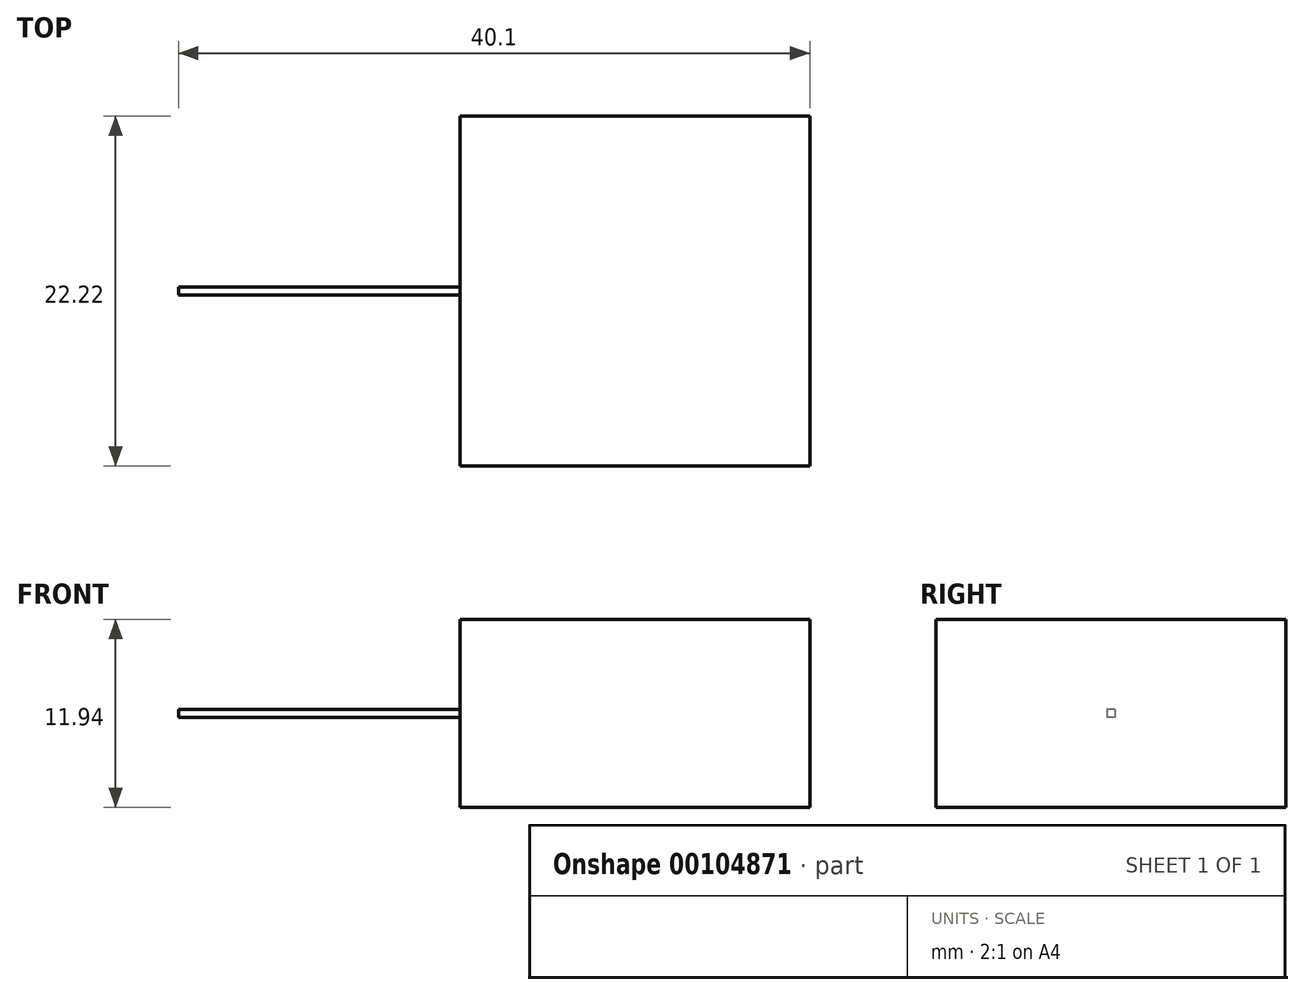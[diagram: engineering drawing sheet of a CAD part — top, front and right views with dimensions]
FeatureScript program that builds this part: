
annotation { "Feature Type Name" : "Feature", "Feature Type Description" : "" }
export const myFeature = defineFeature(function(context is Context, id is Id, definition is map)
    precondition{}
    {
        {
            var Q0;
            Q0=qCreatedBy(makeId("Top.planeOp"),FACE);
            var sketch = newSketch(context, id + "F0", { "sketchPlane" : qUnion([Q0])});
            skLineSegment(sketch, "E0.bottom", {"start": v(-11.11, 11.11) * mm, "end": v(11.11, 11.11) * mm});
            skLineSegment(sketch, "E0.top", {"start": v(-11.11, -11.11) * mm, "end": v(11.11, -11.11) * mm});
            skLineSegment(sketch, "E0.left", {"start": v(-11.11, 11.11) * mm, "end": v(-11.11, -11.11) * mm});
            skLineSegment(sketch, "E0.right", {"start": v(11.11, 11.11) * mm, "end": v(11.11, -11.11) * mm});
            skPoint(sketch, "E0.middle", {"position": v(0, 0) * mm});
            skPoint(sketch, "E1.endSnap0", {"position": v(-11.11, 0) * mm});
            skLineSegment(sketch, "E2", {"start": v(-28.99, 0) * mm, "end": v(-28.99, 0.25) * mm});
            skLineSegment(sketch, "E3", {"start": v(-28.99, 0) * mm, "end": v(-28.99, -0.25) * mm});
            skLineSegment(sketch, "E4.bottom", {"start": v(-28.99, 0.25) * mm, "end": v(-11.11, 0.25) * mm});
            skLineSegment(sketch, "E4.top", {"start": v(-28.99, -0.25) * mm, "end": v(-11.11, -0.25) * mm});
            skLineSegment(sketch, "E4.left", {"start": v(-28.99, 0.25) * mm, "end": v(-28.99, -0.25) * mm});
            skLineSegment(sketch, "E4.right", {"start": v(-11.11, 0.25) * mm, "end": v(-11.11, -0.25) * mm});
            skSolve(sketch);
        }
        {
            var Q0;
            {var subQ3=sQuery(id+"F0.wireOp",EDGE,"E0.bottom");Q0=makeQuery(id+"F0.imprint","IMPRINT",FACE,{"disambiguationData":[TD([[makeQuery(id+"F0.imprint","IMPRINT",EDGE,{"derivedFrom":subQ3}),-1.0]])]});}
            extrude(context, id + "F1", {"entities" : qUnion([Q0]), "endBound" : BoundingType.SYMMETRIC, "depth" : 11.94 * mm});
        }
        {
            var Q0;
            {var subQ0=sQuery(id+"F0.wireOp",EDGE,"E4.bottom");Q0=makeQuery(id+"F0.imprint","IMPRINT",FACE,{"disambiguationData":[TD([[makeQuery(id+"F0.imprint","IMPRINT",EDGE,{"derivedFrom":subQ0}),-1.0]])]});}
            extrude(context, id + "F2", {"entities" : qUnion([Q0]), "operationType" : NewBodyOperationType.ADD, "endBound" : BoundingType.SYMMETRIC, "depth" : 0.5 * mm});
        }
    });
